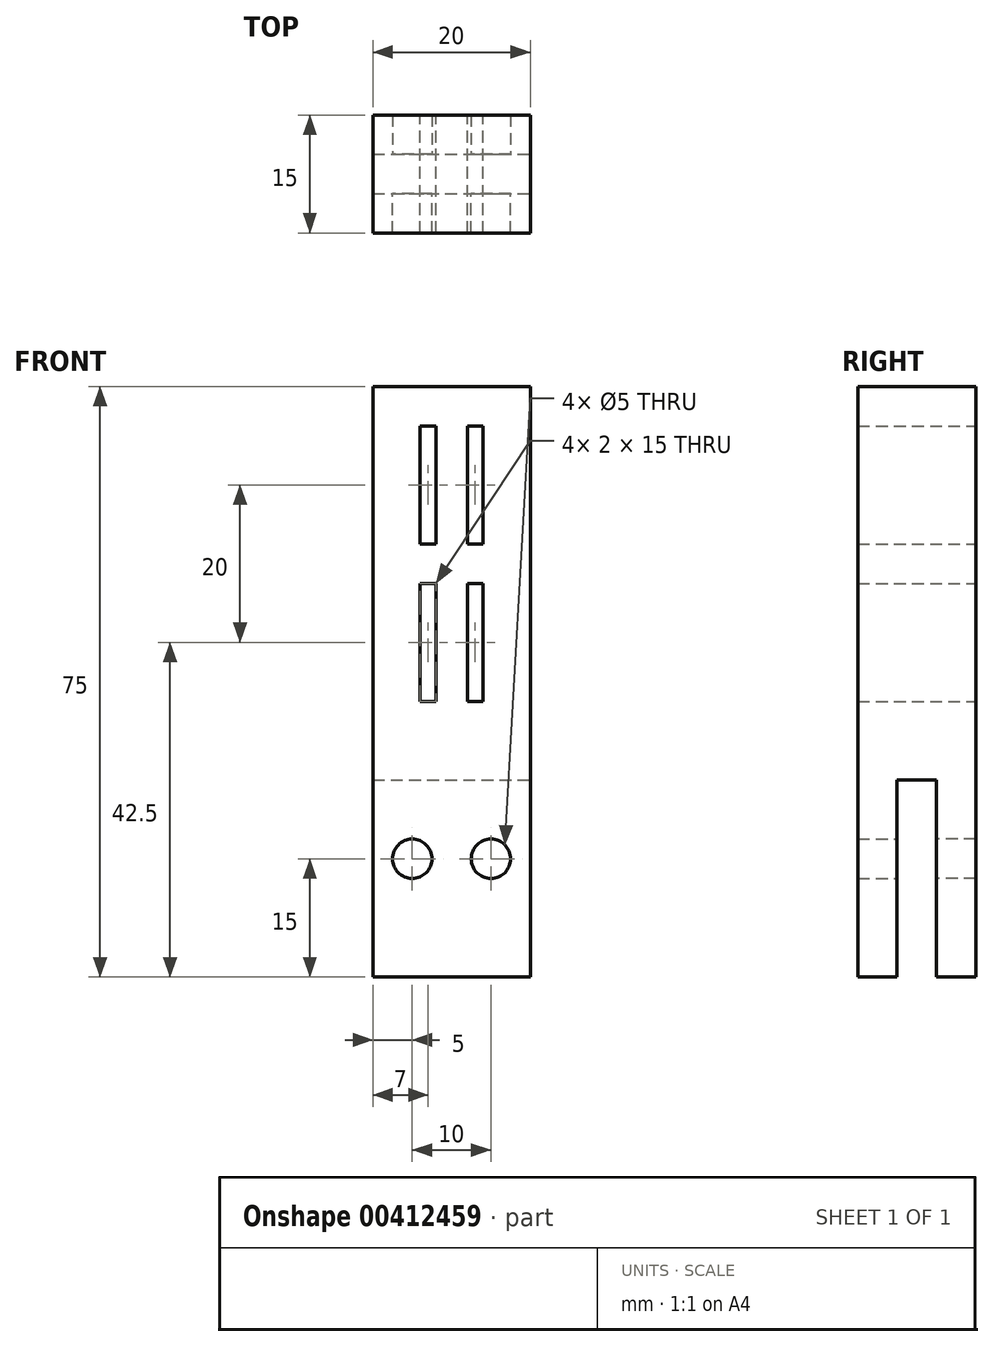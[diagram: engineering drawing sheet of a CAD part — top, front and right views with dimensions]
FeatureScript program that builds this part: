
annotation { "Feature Type Name" : "Feature", "Feature Type Description" : "" }
export const myFeature = defineFeature(function(context is Context, id is Id, definition is map)
    precondition{}
    {
        {
            var Q0;
            Q0=qCreatedBy(makeId("Front.planeOp"),FACE);
            var sketch = newSketch(context, id + "F0", { "sketchPlane" : qUnion([Q0])});
            skLineSegment(sketch, "E0.bottom", {"start": v(10, 35) * mm, "end": v(-10, 35) * mm});
            skLineSegment(sketch, "E0.top", {"start": v(10, -35) * mm, "end": v(-10, -35) * mm});
            skLineSegment(sketch, "E0.left", {"start": v(10, 35) * mm, "end": v(10, -35) * mm});
            skLineSegment(sketch, "E0.right", {"start": v(-10, 35) * mm, "end": v(-10, 17) * mm});
            skPoint(sketch, "E0.middle", {"position": v(0, 0) * mm});
            skLineSegment(sketch, "E1", {"start": v(-10, -10) * mm, "end": v(10, -10) * mm});
            skPoint(sketch, "E2", {"position": v(-5, -25) * mm});
            skPoint(sketch, "E3", {"position": v(5, -25) * mm});
            skCircle(sketch, "E4", {"center": v(-5, -25) * mm, "radius": 2.5 * mm});
            skCircle(sketch, "E5", {"center": v(5, -25) * mm, "radius": 2.5 * mm});
            skLineSegment(sketch, "E6", {"start": v(-10, -15) * mm, "end": v(10, -15) * mm});
            skLineSegment(sketch, "E7.trimOffspring", {"start": v(-10, 15) * mm, "end": v(-10, -35) * mm});
            skLineSegment(sketch, "E8", {"start": v(-10, 17) * mm, "end": v(-10, 15) * mm});
            skLineSegment(sketch, "E9.bottom", {"start": v(-4, 30) * mm, "end": v(-2, 30) * mm});
            skLineSegment(sketch, "E9.top", {"start": v(-4, 15) * mm, "end": v(-2, 15) * mm});
            skLineSegment(sketch, "E9.left", {"start": v(-4, 30) * mm, "end": v(-4, 15) * mm});
            skLineSegment(sketch, "E9.right", {"start": v(-2, 30) * mm, "end": v(-2, 15) * mm});
            skLineSegment(sketch, "E10.bottom", {"start": v(-4, 10) * mm, "end": v(-2, 10) * mm});
            skLineSegment(sketch, "E10.top", {"start": v(-4, -5) * mm, "end": v(-2, -5) * mm});
            skLineSegment(sketch, "E10.left", {"start": v(-4, 10) * mm, "end": v(-4, -5) * mm});
            skLineSegment(sketch, "E10.right", {"start": v(-2, 10) * mm, "end": v(-2, -5) * mm});
            skLineSegment(sketch, "E11.MirrorCS", {"start": v(4, 30) * mm, "end": v(2, 30) * mm});
            skLineSegment(sketch, "E12.MirrorCS", {"start": v(4, 15) * mm, "end": v(2, 15) * mm});
            skLineSegment(sketch, "E13.MirrorCS", {"start": v(4, 30) * mm, "end": v(4, 15) * mm});
            skLineSegment(sketch, "E14.MirrorCS", {"start": v(2, 30) * mm, "end": v(2, 15) * mm});
            skLineSegment(sketch, "E15.MirrorCS", {"start": v(4, -5) * mm, "end": v(2, -5) * mm});
            skLineSegment(sketch, "E16.MirrorCS", {"start": v(4, 10) * mm, "end": v(2, 10) * mm});
            skLineSegment(sketch, "E17.MirrorCS", {"start": v(4, 10) * mm, "end": v(4, -5) * mm});
            skLineSegment(sketch, "E18.MirrorCS", {"start": v(2, 10) * mm, "end": v(2, -5) * mm});
            skLineSegment(sketch, "E19.0", {"start": v(10, -40) * mm, "end": v(-10, -40) * mm});
            skLineSegment(sketch, "E20", {"start": v(-10, -40) * mm, "end": v(-10, -35) * mm});
            skLineSegment(sketch, "E21", {"start": v(10, -40) * mm, "end": v(10, -35) * mm});
            skSolve(sketch);
        }
        {
            var Q0;
            {var subQ0=sQuery(id+"F0.wireOp",EDGE,"E0.bottom");Q0=makeQuery(id+"F0.imprint","IMPRINT",FACE,{"disambiguationData":[TD([[makeQuery(id+"F0.imprint","IMPRINT",EDGE,{"derivedFrom":subQ0}),1.0]])]});}
            var Q1;
            {var subQ0=sQuery(id+"F0.wireOp",EDGE,"E1");Q1=makeQuery(id+"F0.imprint","IMPRINT",FACE,{"disambiguationData":[TD([[makeQuery(id+"F0.imprint","IMPRINT",EDGE,{"derivedFrom":subQ0}),-1.0]])]});}
            extrude(context, id + "F1", {"entities" : qUnion([Q0, Q1]), "endBound" : BoundingType.SYMMETRIC, "depth" : 15 * mm});
        }
        {
            var Q0;
            {var subQ0=sQuery(id+"F0.wireOp",EDGE,"E1");Q0=makeQuery(id+"F0.imprint","IMPRINT",FACE,{"disambiguationData":[TD([[makeQuery(id+"F0.imprint","IMPRINT",EDGE,{"derivedFrom":subQ0}),-1.0]])]});}
            var Q1;
            {var subQ1=sQuery(id+"F0.wireOp",EDGE,"E0.top");Q1=makeQuery(id+"F0.imprint","IMPRINT",FACE,{"disambiguationData":[TD([[makeQuery(id+"F0.imprint","IMPRINT",EDGE,{"derivedFrom":subQ1}),-1.0]])]});}
            var Q2;
            Q2=makeQuery(id+"F0.imprint","IMPRINT",FACE,{"disambiguationData":[TD([[makeQuery(id+"F0.imprint","IMPRINT",EDGE,{"derivedFrom":sQuery(id+"F0.wireOp",EDGE,"E0.top")}),1.0]])]});
            extrude(context, id + "F2", {"entities" : qUnion([Q0, Q1, Q2]), "operationType" : NewBodyOperationType.ADD, "depth" : 7.5 * mm, "hasSecondDirection" : true, "secondDirectionOppositeDirection" : false, "secondDirectionDepth" : 2.5 * mm});
        }
        {
            var Q0;
            {var subQ0=sQuery(id+"F0.wireOp",EDGE,"E1");Q0=makeQuery(id+"F0.imprint","IMPRINT",FACE,{"disambiguationData":[TD([[makeQuery(id+"F0.imprint","IMPRINT",EDGE,{"derivedFrom":subQ0}),-1.0]])]});}
            var Q1;
            {var subQ1=sQuery(id+"F0.wireOp",EDGE,"E0.top");Q1=makeQuery(id+"F0.imprint","IMPRINT",FACE,{"disambiguationData":[TD([[makeQuery(id+"F0.imprint","IMPRINT",EDGE,{"derivedFrom":subQ1}),-1.0]])]});}
            var Q2;
            Q2=makeQuery(id+"F0.imprint","IMPRINT",FACE,{"disambiguationData":[TD([[makeQuery(id+"F0.imprint","IMPRINT",EDGE,{"derivedFrom":sQuery(id+"F0.wireOp",EDGE,"E0.top")}),1.0]])]});
            extrude(context, id + "F3", {"entities" : qUnion([Q0, Q1, Q2]), "operationType" : NewBodyOperationType.ADD, "oppositeDirection" : true, "depth" : 7.5 * mm, "hasSecondDirection" : true, "secondDirectionOppositeDirection" : true, "secondDirectionDepth" : 2.5 * mm});
        }
    });
